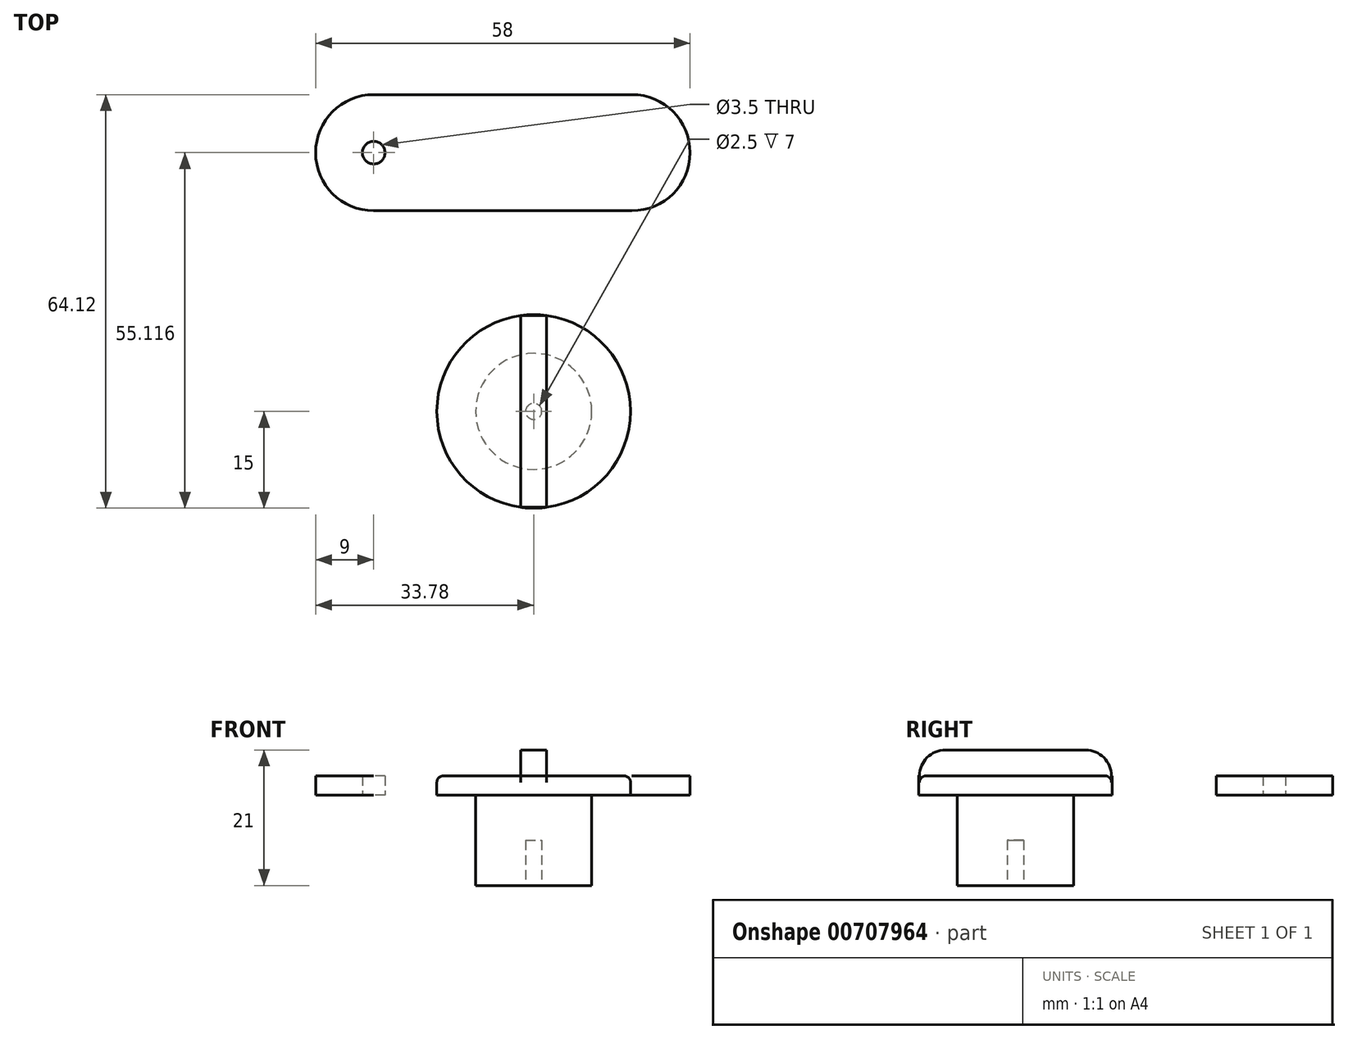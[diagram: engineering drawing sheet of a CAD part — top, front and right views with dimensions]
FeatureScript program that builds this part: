
annotation { "Feature Type Name" : "Feature", "Feature Type Description" : "" }
export const myFeature = defineFeature(function(context is Context, id is Id, definition is map)
    precondition{}
    {
        {
            var Q0;
            Q0=qCreatedBy(makeId("Top.planeOp"),FACE);
            var sketch = newSketch(context, id + "F0", { "sketchPlane" : qUnion([Q0])});
            skCircle(sketch, "E0", {"center": v(0, 0) * mm, "radius": 15 * mm});
            skSolve(sketch);
        }
        {
            var Q0;
            Q0=makeQuery(id+"F0.imprint","IMPRINT",FACE,{"disambiguationData":[TD([[makeQuery(id+"F0.imprint","IMPRINT",EDGE,{"derivedFrom":sQuery(id+"F0.wireOp",EDGE,"E0")}),1.0]])]});
            extrude(context, id + "F1", {"entities" : qUnion([Q0]), "depth" : 3 * mm, "offsetDistance" : 25 * mm});
        }
        {
            var Q0;
            Q0=makeQuery(id+"F1.opExtrude","CAP_FACE",FACE,{"disambiguationData":[OSD([sQuery(id+"F0.wireOp",EDGE,"E0")])],"isStart":true});
            var sketch = newSketch(context, id + "F2", { "sketchPlane" : qUnion([Q0])});
            skCircle(sketch, "E1", {"center": v(0, 0) * mm, "radius": 9 * mm});
            skSolve(sketch);
        }
        {
            var Q0;
            Q0=makeQuery(id+"F2.imprint","IMPRINT",FACE,{"disambiguationData":[TD([[makeQuery(id+"F2.imprint","IMPRINT",EDGE,{"derivedFrom":sQuery(id+"F2.wireOp",EDGE,"E1")}),1.0]])]});
            extrude(context, id + "F3", {"entities" : qUnion([Q0]), "operationType" : NewBodyOperationType.ADD, "depth" : 14 * mm, "offsetDistance" : 25 * mm});
        }
        {
            var Q0;
            Q0=makeQuery(id+"F1.opExtrude","CAP_FACE",FACE,{"disambiguationData":[OSD([sQuery(id+"F0.wireOp",EDGE,"E0")])],"isStart":false});
            var sketch = newSketch(context, id + "F4", { "sketchPlane" : qUnion([Q0])});
            skLineSegment(sketch, "E2.bottom", {"start": v(-2, 14.87) * mm, "end": v(2, 14.87) * mm});
            skLineSegment(sketch, "E2.top", {"start": v(-2, -14.87) * mm, "end": v(2, -14.87) * mm});
            skLineSegment(sketch, "E2.left", {"start": v(-2, 14.87) * mm, "end": v(-2, -14.87) * mm});
            skLineSegment(sketch, "E2.right", {"start": v(2, 14.87) * mm, "end": v(2, -14.87) * mm});
            skSolve(sketch);
        }
        {
            var Q0;
            Q0=makeQuery(id+"F4.imprint","IMPRINT",FACE,{"disambiguationData":[TD([[makeQuery(id+"F4.imprint","IMPRINT",EDGE,{"derivedFrom":sQuery(id+"F4.wireOp",EDGE,"E2.bottom")}),-1.0]])]});
            extrude(context, id + "F5", {"entities" : qUnion([Q0]), "operationType" : NewBodyOperationType.ADD, "depth" : 4 * mm, "offsetDistance" : 25 * mm});
        }
        {
            var Q0;
            Q0=makeQuery(id+"F5.opExtrude","CAP_EDGE",EDGE,{"disambiguationData":[OSD([sQuery(id+"F4.wireOp",EDGE,"E2.bottom")])],"isStart":false});
            var Q1;
            Q1=makeQuery(id+"F5.opExtrude","CAP_EDGE",EDGE,{"disambiguationData":[OSD([sQuery(id+"F4.wireOp",EDGE,"E2.top")])],"isStart":false});
            fillet(context, id + "F6", {"entities" : qUnion([Q0, Q1]), "radius" : 4 * mm, "tangentPropagation" : true, "allowEdgeOverflow" : false});
        }
        {
            var Q0;
            {var subQ0=sQuery(id+"F0.wireOp",EDGE,"E0");Q0=makeQuery(id+"F5.boolean.opBoolean","SPLIT",EDGE,{"disambiguationData":[TD([makeQuery(id+"F1.opExtrude","SWEPT_FACE",FACE,{"disambiguationData":[OSD([subQ0])]}),makeQuery(id+"F1.opExtrude","CAP_FACE",FACE,{"disambiguationData":[OSD([subQ0])],"isStart":false}),makeQuery(id+"F5.opExtrude","SWEPT_FACE",FACE,{"disambiguationData":[OSD([sQuery(id+"F4.wireOp",EDGE,"E2.bottom")])]}),makeQuery(id+"F5.opExtrude","SWEPT_FACE",FACE,{"disambiguationData":[OSD([sQuery(id+"F4.wireOp",EDGE,"E2.top")])]}),makeQuery(id+"F5.opExtrude","SWEPT_FACE",FACE,{"disambiguationData":[OSD([sQuery(id+"F4.wireOp",EDGE,"E2.left")])]})])],"derivedFrom":makeQuery(id+"F1.opExtrude","CAP_EDGE",EDGE,{"disambiguationData":[OSD([subQ0])],"isStart":false})});}
            var Q1;
            {var subQ0=sQuery(id+"F0.wireOp",EDGE,"E0");Q1=makeQuery(id+"F5.boolean.opBoolean","SPLIT",EDGE,{"disambiguationData":[TD([makeQuery(id+"F1.opExtrude","SWEPT_FACE",FACE,{"disambiguationData":[OSD([subQ0])]}),makeQuery(id+"F1.opExtrude","CAP_FACE",FACE,{"disambiguationData":[OSD([subQ0])],"isStart":false}),makeQuery(id+"F5.opExtrude","SWEPT_FACE",FACE,{"disambiguationData":[OSD([sQuery(id+"F4.wireOp",EDGE,"E2.bottom")])]}),makeQuery(id+"F5.opExtrude","SWEPT_FACE",FACE,{"disambiguationData":[OSD([sQuery(id+"F4.wireOp",EDGE,"E2.top")])]}),makeQuery(id+"F5.opExtrude","SWEPT_FACE",FACE,{"disambiguationData":[OSD([sQuery(id+"F4.wireOp",EDGE,"E2.right")])]})])],"derivedFrom":makeQuery(id+"F1.opExtrude","CAP_EDGE",EDGE,{"disambiguationData":[OSD([subQ0])],"isStart":false})});}
            fillet(context, id + "F7", {"entities" : qUnion([Q0, Q1]), "radius" : 1 * mm, "tangentPropagation" : true, "allowEdgeOverflow" : false});
        }
        {
            var Q0;
            Q0=makeQuery(id+"F3.opExtrude","CAP_FACE",FACE,{"disambiguationData":[OSD([sQuery(id+"F2.wireOp",EDGE,"E1")])],"isStart":false});
            var sketch = newSketch(context, id + "F8", { "sketchPlane" : qUnion([Q0])});
            skCircle(sketch, "E3", {"center": v(0, 0) * mm, "radius": 1.25 * mm});
            skSolve(sketch);
        }
        {
            var Q0;
            Q0=makeQuery(id+"F8.imprint","IMPRINT",FACE,{"disambiguationData":[TD([[makeQuery(id+"F8.imprint","IMPRINT",EDGE,{"derivedFrom":sQuery(id+"F8.wireOp",EDGE,"E3")}),1.0]])]});
            extrude(context, id + "F9", {"entities" : qUnion([Q0]), "operationType" : NewBodyOperationType.REMOVE, "oppositeDirection" : true, "depth" : 7 * mm, "offsetDistance" : 25 * mm});
        }
        {
            var Q0;
            Q0=qCreatedBy(makeId("Top.planeOp"),FACE);
            var sketch = newSketch(context, id + "F10", { "sketchPlane" : qUnion([Q0])});
            skLineSegment(sketch, "E4.bottom", {"start": v(-33.78, 49.12) * mm, "end": v(24.22, 49.12) * mm});
            skLineSegment(sketch, "E4.top", {"start": v(-33.78, 31.12) * mm, "end": v(24.22, 31.12) * mm});
            skLineSegment(sketch, "E4.left", {"start": v(-33.78, 49.12) * mm, "end": v(-33.78, 31.12) * mm});
            skLineSegment(sketch, "E4.right", {"start": v(24.22, 49.12) * mm, "end": v(24.22, 31.12) * mm});
            skCircle(sketch, "E5", {"center": v(-24.78, 40.12) * mm, "radius": 1.75 * mm});
            skSolve(sketch);
        }
        {
            var Q0;
            Q0=makeQuery(id+"F10.imprint","IMPRINT",FACE,{"disambiguationData":[TD([[makeQuery(id+"F10.imprint","IMPRINT",EDGE,{"derivedFrom":sQuery(id+"F10.wireOp",EDGE,"E4.bottom")}),-1.0]])]});
            extrude(context, id + "F11", {"entities" : qUnion([Q0]), "depth" : 3 * mm, "offsetDistance" : 25 * mm});
        }
        {
            var Q0;
            Q0=makeQuery(id+"F11.opExtrude","SWEPT_EDGE",EDGE,{"disambiguationData":[OSD([sQuery(id+"F10.wireOp",EDGE,"E4.bottom"),sQuery(id+"F10.wireOp",EDGE,"E4.left")])]});
            var Q1;
            Q1=makeQuery(id+"F11.opExtrude","SWEPT_EDGE",EDGE,{"disambiguationData":[OSD([sQuery(id+"F10.wireOp",EDGE,"E4.top"),sQuery(id+"F10.wireOp",EDGE,"E4.left")])]});
            var Q2;
            Q2=makeQuery(id+"F11.opExtrude","SWEPT_EDGE",EDGE,{"disambiguationData":[OSD([sQuery(id+"F10.wireOp",EDGE,"E4.bottom"),sQuery(id+"F10.wireOp",EDGE,"E4.right")])]});
            var Q3;
            Q3=makeQuery(id+"F11.opExtrude","SWEPT_EDGE",EDGE,{"disambiguationData":[OSD([sQuery(id+"F10.wireOp",EDGE,"E4.top"),sQuery(id+"F10.wireOp",EDGE,"E4.right")])]});
            fillet(context, id + "F12", {"entities" : qUnion([Q0, Q1, Q2, Q3]), "radius" : 9 * mm, "tangentPropagation" : true, "allowEdgeOverflow" : false});
        }
    });
